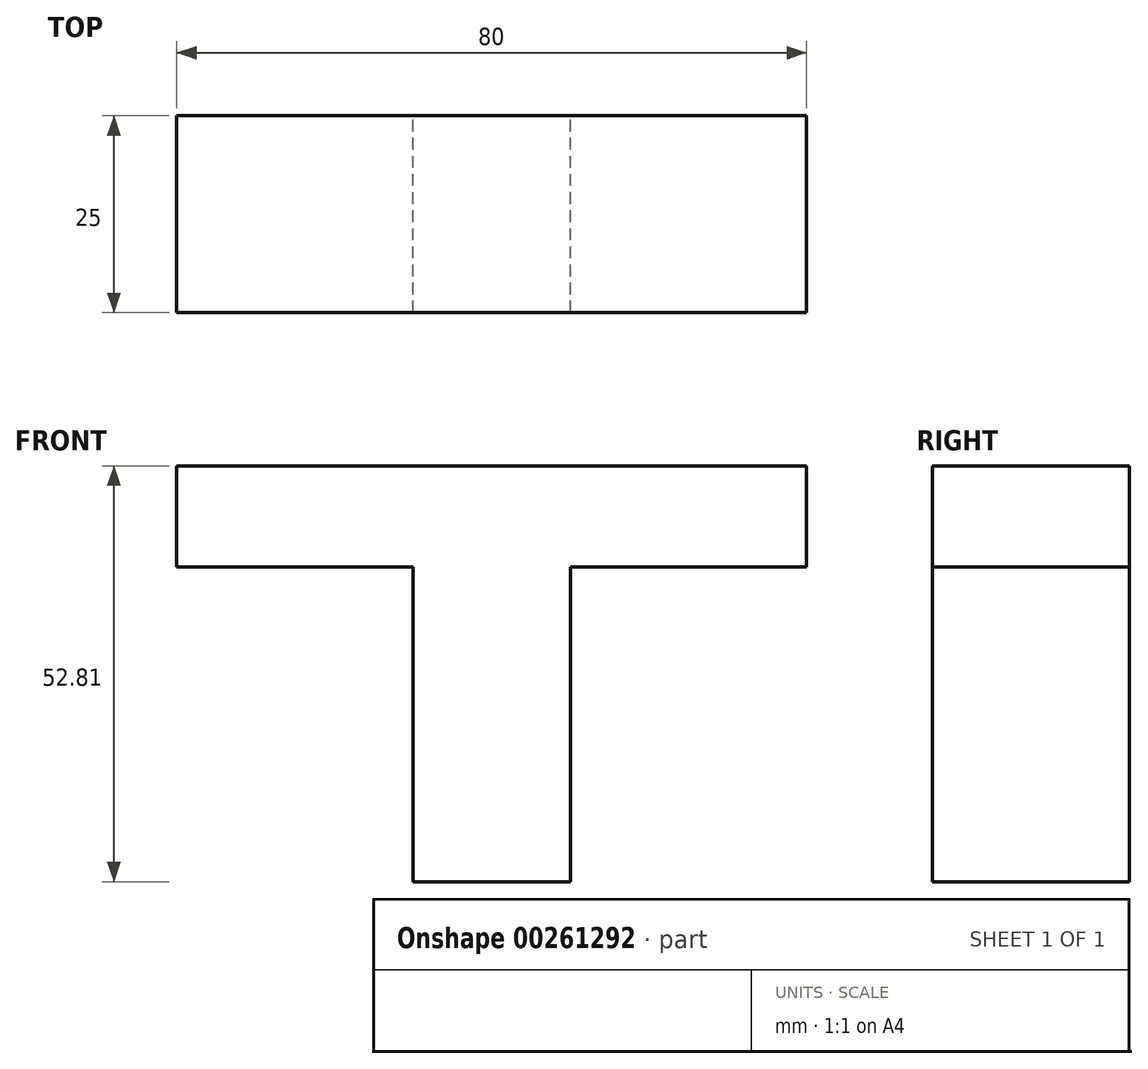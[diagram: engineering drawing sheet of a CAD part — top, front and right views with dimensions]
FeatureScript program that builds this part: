
annotation { "Feature Type Name" : "Feature", "Feature Type Description" : "" }
export const myFeature = defineFeature(function(context is Context, id is Id, definition is map)
    precondition{}
    {
        {
            var Q0;
            Q0=qCreatedBy(makeId("Front.planeOp"),FACE);
            var sketch = newSketch(context, id + "F0", { "sketchPlane" : qUnion([Q0])});
            skLineSegment(sketch, "E0", {"start": v(-9.77, -16.14) * mm, "end": v(10.23, -16.14) * mm});
            skLineSegment(sketch, "E1", {"start": v(10.23, -16.14) * mm, "end": v(10.23, 23.86) * mm});
            skLineSegment(sketch, "E2", {"start": v(10.23, 23.86) * mm, "end": v(40.23, 23.86) * mm});
            skLineSegment(sketch, "E3", {"start": v(40.23, 23.86) * mm, "end": v(40.23, 36.67) * mm});
            skLineSegment(sketch, "E4", {"start": v(40.23, 36.67) * mm, "end": v(-39.77, 36.67) * mm});
            skLineSegment(sketch, "E5", {"start": v(-39.77, 36.67) * mm, "end": v(-39.77, 23.86) * mm});
            skLineSegment(sketch, "E6", {"start": v(-39.77, 23.86) * mm, "end": v(-9.77, 23.86) * mm});
            skLineSegment(sketch, "E7", {"start": v(-9.77, 23.86) * mm, "end": v(-9.77, -16.14) * mm});
            skSolve(sketch);
        }
        {
            var Q0;
            Q0=makeQuery(id+"F0.imprint","IMPRINT",FACE,{"disambiguationData":[TD([[makeQuery(id+"F0.imprint","IMPRINT",EDGE,{"derivedFrom":sQuery(id+"F0.wireOp",EDGE,"E0")}),1.0]])]});
            extrude(context, id + "F1", {"entities" : qUnion([Q0]), "depth" : 25 * mm});
        }
    });
